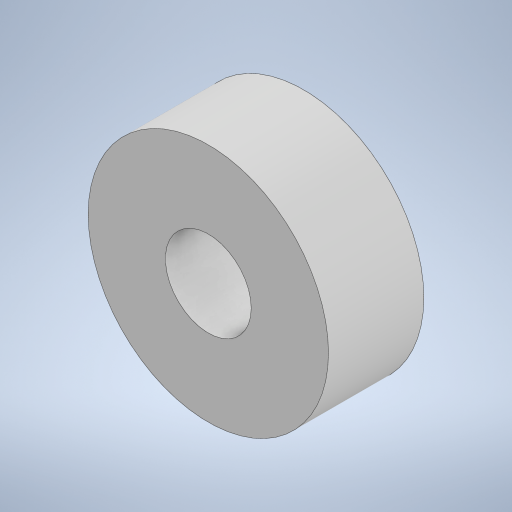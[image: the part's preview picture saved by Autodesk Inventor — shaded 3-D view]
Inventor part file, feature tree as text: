
AUTODESK INVENTOR PART (.ipt)
format: ipt  version: 2024 (Build 280153000, 153)  size: 212,480 bytes
history: native  units: mm
features: extrude x1, sketch x1
ambient origin geometry x8: Origin, YZ Plane, XZ Plane, XY Plane, X Axis, Y Axis, Z Axis, Center Point
bodies: Solid1 (feature_tree)
feature tree (2):
  extrude  "Extrusion1"  Depth=5.0mm
  sketch  "Sketch1"  dims[d0=12.6mm d1=4.5mm d2=5.0mm d3=0.0mm]
